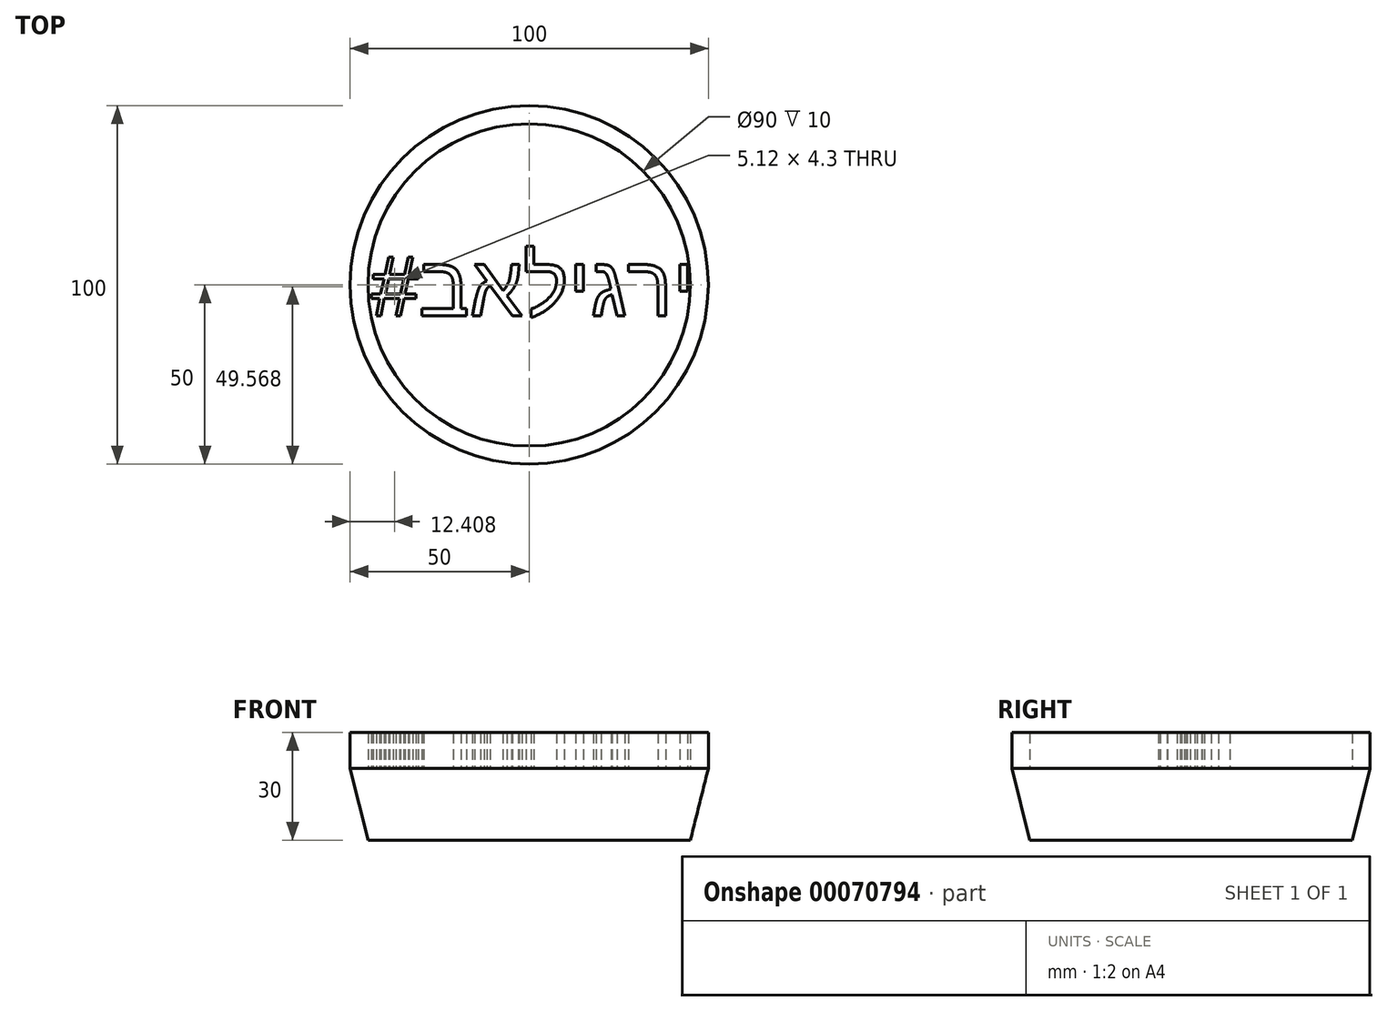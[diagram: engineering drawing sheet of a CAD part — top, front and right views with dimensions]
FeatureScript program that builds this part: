
annotation { "Feature Type Name" : "Feature", "Feature Type Description" : "" }
export const myFeature = defineFeature(function(context is Context, id is Id, definition is map)
    precondition{}
    {
        {
            var Q0;
            Q0=qCreatedBy(makeId("Top.planeOp"),FACE);
            var sketch = newSketch(context, id + "F0", { "sketchPlane" : qUnion([Q0])});
            skCircle(sketch, "E0", {"center": v(0, 0) * mm, "radius": 50 * mm});
            skCircle(sketch, "E1", {"center": v(0, 0) * mm, "radius": 45 * mm});
            skLineSegment(sketch, "E2", {"start": v(45, 0) * mm, "end": v(-45, 0) * mm, "construction": true});
            skLineSegment(sketch, "E3", {"start": v(-44.17, 0) * mm, "end": v(-44.17, -8.59) * mm, "construction": true});
            skLineSegment(sketch, "E4", {"start": v(-44.17, 0) * mm, "end": v(-44.17, 8.59) * mm, "construction": true});
            skLineSegment(sketch, "E5", {"start": v(-44.17, 8.59) * mm, "end": v(44.17, 8.59) * mm, "construction": true});
            skLineSegment(sketch, "E6", {"start": v(44.17, 8.59) * mm, "end": v(44.17, -8.59) * mm, "construction": true});
            skLineSegment(sketch, "E7", {"start": v(44.17, -8.59) * mm, "end": v(-44.17, -8.59) * mm, "construction": true});
            skText(sketch, "E8", { "text": "#באליגרי\n", "fontName": "Arimo-Regular.ttf"});
            const initialGuessF0  = {"E8": [-0.04417, -0.00859, 1, 0, 0.01717]};
            skSetInitialGuess(sketch, initialGuessF0);
            skSolve(sketch);
        }
        {
            var Q0;
            Q0 = qSketchRegion(id + "F0", true);
            var Q1;
            Q1=makeQuery(id+"F0.imprint","IMPRINT",FACE,{"disambiguationData":[TD([[makeQuery(id+"F0.imprint","IMPRINT",EDGE,{"derivedFrom":sQuery(id+"F0.wireOp",EDGE,"E8.sketch_text.stroke-0")}),-1.0]])]});
            var Q2;
            Q2=makeQuery(id+"F0.imprint","IMPRINT",FACE,{"disambiguationData":[TD([[makeQuery(id+"F0.imprint","IMPRINT",EDGE,{"derivedFrom":sQuery(id+"F0.wireOp",EDGE,"E8.sketch_text.stroke-32")}),-1.0]])]});
            var Q3;
            Q3=makeQuery(id+"F0.imprint","IMPRINT",FACE,{"disambiguationData":[TD([[makeQuery(id+"F0.imprint","IMPRINT",EDGE,{"derivedFrom":sQuery(id+"F0.wireOp",EDGE,"E8.sketch_text.stroke-46")}),-1.0]])]});
            var Q4;
            Q4=makeQuery(id+"F0.imprint","IMPRINT",FACE,{"disambiguationData":[TD([[makeQuery(id+"F0.imprint","IMPRINT",EDGE,{"derivedFrom":sQuery(id+"F0.wireOp",EDGE,"E8.sketch_text.stroke-68")}),-1.0]])]});
            var Q5;
            Q5=makeQuery(id+"F0.imprint","IMPRINT",FACE,{"disambiguationData":[TD([[makeQuery(id+"F0.imprint","IMPRINT",EDGE,{"derivedFrom":sQuery(id+"F0.wireOp",EDGE,"E8.sketch_text.stroke-81")}),-1.0]])]});
            var Q6;
            Q6=makeQuery(id+"F0.imprint","IMPRINT",FACE,{"disambiguationData":[TD([[makeQuery(id+"F0.imprint","IMPRINT",EDGE,{"derivedFrom":sQuery(id+"F0.wireOp",EDGE,"E8.sketch_text.stroke-85")}),-1.0]])]});
            var Q7;
            Q7=makeQuery(id+"F0.imprint","IMPRINT",FACE,{"disambiguationData":[TD([[makeQuery(id+"F0.imprint","IMPRINT",EDGE,{"derivedFrom":sQuery(id+"F0.wireOp",EDGE,"E8.sketch_text.stroke-108")}),-1.0]])]});
            var Q8;
            Q8=makeQuery(id+"F0.imprint","IMPRINT",FACE,{"disambiguationData":[TD([[makeQuery(id+"F0.imprint","IMPRINT",EDGE,{"derivedFrom":sQuery(id+"F0.wireOp",EDGE,"E8.sketch_text.stroke-118")}),-1.0]])]});
            extrude(context, id + "F1", {"entities" : qUnion([Q0, Q1, Q2, Q3, Q4, Q5, Q6, Q7, Q8]), "depth" : 10 * mm});
        }
        {
            var Q0;
            Q0=qCreatedBy(makeId("Top.planeOp"),FACE);
            var sketch = newSketch(context, id + "F2", { "sketchPlane" : qUnion([Q0])});
            skCircle(sketch, "E9.0", {"center": v(0, 0) * mm, "radius": 50 * mm});
            skPoint(sketch, "E10", {"position": v(-35.95, -34.75) * mm});
            skSolve(sketch);
        }
        {
            var Q0;
            Q0=qCreatedBy(makeId("Top.planeOp"),FACE);
            cPlane(context, id + "F3", {"entities" : qUnion([Q0]), "cplaneType" : CPlaneType.OFFSET, "offset" : 20 * mm, "oppositeDirection" : true, "width" : 150 * mm, "height" : 150 * mm});
        }
        {
            var Q0;
            Q0=qCreatedBy(id+"F3.planeOp",FACE);
            var sketch = newSketch(context, id + "F4", { "sketchPlane" : qUnion([Q0])});
            skCircle(sketch, "E11.0", {"center": v(0, 0) * mm, "radius": 45 * mm});
            skSolve(sketch);
        }
        {
            var Q0;
            Q0 = qSketchRegion(id + "F2", true);
            var Q1;
            Q1 = qSketchRegion(id + "F4", true);
            loft(context, id + "F5", {"sheetProfilesArray" : [{ "sheetProfileEntities" : qUnion([Q0]) }, { "sheetProfileEntities" : qUnion([Q1]) }]});
        }
    });
